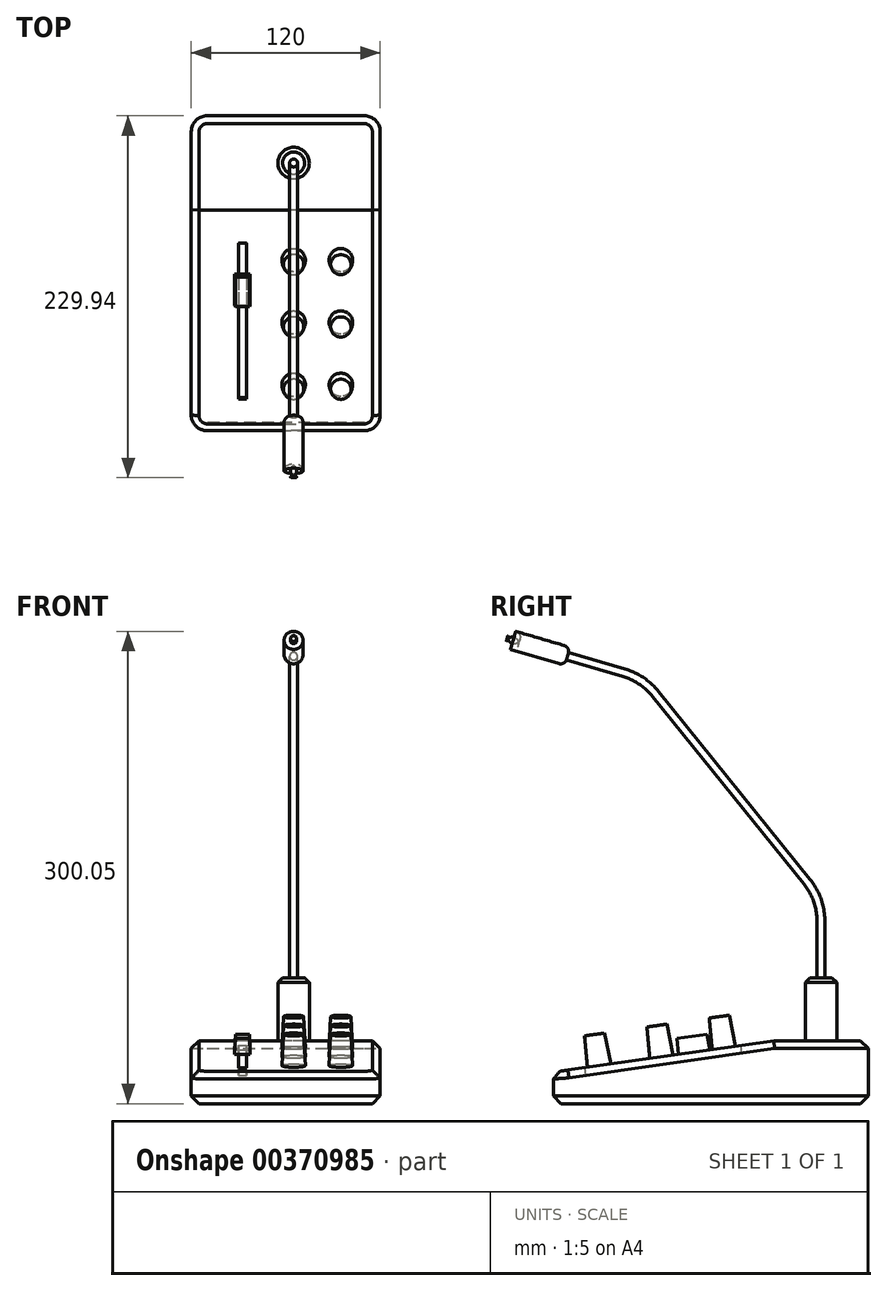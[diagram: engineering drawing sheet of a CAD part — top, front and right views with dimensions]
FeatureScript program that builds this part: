
annotation { "Feature Type Name" : "Feature", "Feature Type Description" : "" }
export const myFeature = defineFeature(function(context is Context, id is Id, definition is map)
    precondition{}
    {
        {
            var Q0;
            Q0=qCreatedBy(makeId("Right.planeOp"),FACE);
            var sketch = newSketch(context, id + "F0", { "sketchPlane" : qUnion([Q0])});
            skLineSegment(sketch, "E0", {"start": v(-86.5, 0) * mm, "end": v(113.5, 0) * mm});
            skLineSegment(sketch, "E1", {"start": v(113.5, 0) * mm, "end": v(113.5, 40) * mm});
            skLineSegment(sketch, "E2", {"start": v(113.5, 40) * mm, "end": v(53.5, 40) * mm});
            skLineSegment(sketch, "E3", {"start": v(53.5, 40) * mm, "end": v(-86.5, 20) * mm});
            skLineSegment(sketch, "E4", {"start": v(-86.5, 20) * mm, "end": v(-86.5, 0) * mm});
            skSolve(sketch);
        }
        {
            var Q0;
            Q0 = qSketchRegion(id + "F0", true);
            extrude(context, id + "F1", {"entities" : qUnion([Q0]), "endBound" : BoundingType.SYMMETRIC, "depth" : 120 * mm});
        }
        {
            var Q0;
            Q0=makeQuery(id+"F1.opExtrude","CAP_EDGE",EDGE,{"disambiguationData":[OSD([sQuery(id+"F0.wireOp",EDGE,"E4")])],"isStart":true});
            var Q1;
            Q1=makeQuery(id+"F1.opExtrude","CAP_EDGE",EDGE,{"disambiguationData":[OSD([sQuery(id+"F0.wireOp",EDGE,"E4")])],"isStart":false});
            var Q2;
            Q2=makeQuery(id+"F1.opExtrude","CAP_EDGE",EDGE,{"disambiguationData":[OSD([sQuery(id+"F0.wireOp",EDGE,"E1")])],"isStart":false});
            var Q3;
            Q3=makeQuery(id+"F1.opExtrude","CAP_EDGE",EDGE,{"disambiguationData":[OSD([sQuery(id+"F0.wireOp",EDGE,"E1")])],"isStart":true});
            fillet(context, id + "F2", {"entities" : qUnion([Q0, Q1, Q2, Q3]), "radius" : 10 * mm, "tangentPropagation" : true, "allowEdgeOverflow" : false});
        }
        {
            var Q0;
            Q0=makeQuery(id+"F1.opExtrude","CAP_EDGE",EDGE,{"disambiguationData":[OSD([sQuery(id+"F0.wireOp",EDGE,"E0")])],"isStart":true});
            var Q1;
            Q1=makeQuery(id+"F1.opExtrude","CAP_EDGE",EDGE,{"disambiguationData":[OSD([sQuery(id+"F0.wireOp",EDGE,"E3")])],"isStart":false});
            var Q2;
            Q2=makeQuery(id+"F1.opExtrude","CAP_EDGE",EDGE,{"disambiguationData":[OSD([sQuery(id+"F0.wireOp",EDGE,"E2")])],"isStart":false});
            chamfer(context, id + "F3", {"entities" : qUnion([Q0, Q1, Q2]), "width" : 5 * mm, "tangentPropagation" : true});
        }
        {
            var Q0;
            Q0=makeQuery(id+"F1.opExtrude","SWEPT_FACE",FACE,{"disambiguationData":[OSD([sQuery(id+"F0.wireOp",EDGE,"E3")])]});
            var sketch = newSketch(context, id + "F4", { "sketchPlane" : qUnion([Q0])});
            skLineSegment(sketch, "E5.bottom", {"start": v(-30, 37.58) * mm, "end": v(-25, 37.58) * mm});
            skLineSegment(sketch, "E5.top", {"start": v(-30, -62.42) * mm, "end": v(-25, -62.42) * mm});
            skLineSegment(sketch, "E5.left", {"start": v(-30, 37.58) * mm, "end": v(-30, -62.42) * mm});
            skLineSegment(sketch, "E5.right", {"start": v(-25, 37.58) * mm, "end": v(-25, -62.42) * mm});
            skSolve(sketch);
        }
        {
            var Q0;
            Q0 = qSketchRegion(id + "F4", true);
            extrude(context, id + "F5", {"entities" : qUnion([Q0]), "operationType" : NewBodyOperationType.REMOVE, "oppositeDirection" : true, "depth" : 5 * mm});
        }
        {
            var Q0;
            Q0=makeQuery(id+"F1.opExtrude","SWEPT_FACE",FACE,{"disambiguationData":[OSD([sQuery(id+"F0.wireOp",EDGE,"E3")])]});
            var sketch = newSketch(context, id + "F6", { "sketchPlane" : qUnion([Q0])});
            skLineSegment(sketch, "E6.bottom", {"start": v(-32.5, 17.58) * mm, "end": v(-22.5, 17.58) * mm});
            skLineSegment(sketch, "E6.top", {"start": v(-32.5, -2.42) * mm, "end": v(-22.5, -2.42) * mm});
            skLineSegment(sketch, "E6.left", {"start": v(-32.5, 17.58) * mm, "end": v(-32.5, -2.42) * mm});
            skLineSegment(sketch, "E6.right", {"start": v(-22.5, 17.58) * mm, "end": v(-22.5, -2.42) * mm});
            skSolve(sketch);
        }
        {
            var Q0;
            Q0 = qSketchRegion(id + "F6", true);
            extrude(context, id + "F7", {"entities" : qUnion([Q0]), "operationType" : NewBodyOperationType.ADD, "depth" : 10 * mm, "hasDraft" : true, "draftAngle" : 3 * degree, "draftPullDirection" : true});
        }
        {
            var Q0;
            Q0=makeQuery(id+"F1.opExtrude","SWEPT_FACE",FACE,{"disambiguationData":[OSD([sQuery(id+"F0.wireOp",EDGE,"E3")])]});
            var sketch = newSketch(context, id + "F8", { "sketchPlane" : qUnion([Q0])});
            skCircle(sketch, "E7", {"center": v(35, -53.42) * mm, "radius": 7.5 * mm});
            skCircle(sketch, "E8.0.1.0", {"center": v(35, -13.42) * mm, "radius": 7.5 * mm});
            skCircle(sketch, "E8.0.2.0", {"center": v(35, 26.58) * mm, "radius": 7.5 * mm});
            skCircle(sketch, "E8.1.0.0", {"center": v(5, -53.42) * mm, "radius": 7.5 * mm});
            skCircle(sketch, "E8.1.1.0", {"center": v(5, -13.42) * mm, "radius": 7.5 * mm});
            skCircle(sketch, "E8.1.2.0", {"center": v(5, 26.58) * mm, "radius": 7.5 * mm});
            skLineSegment(sketch, "E8.direction1", {"start": v(35, -53.42) * mm, "end": v(5, -53.42) * mm, "construction": true});
            skLineSegment(sketch, "E8.direction2", {"start": v(35, -53.42) * mm, "end": v(35, -13.42) * mm, "construction": true});
            skSolve(sketch);
        }
        {
            var Q0;
            Q0 = qSketchRegion(id + "F8", true);
            extrude(context, id + "F9", {"entities" : qUnion([Q0]), "operationType" : NewBodyOperationType.ADD, "depth" : 20 * mm, "hasDraft" : true, "draftAngle" : 3 * degree, "draftPullDirection" : true});
        }
        {
            var Q0;
            Q0=makeQuery(id+"F1.opExtrude","SWEPT_FACE",FACE,{"disambiguationData":[OSD([sQuery(id+"F0.wireOp",EDGE,"E2")])]});
            var sketch = newSketch(context, id + "F10", { "sketchPlane" : qUnion([Q0])});
            skCircle(sketch, "E9", {"center": v(5, 83.5) * mm, "radius": 10 * mm});
            skSolve(sketch);
        }
        {
            var Q0;
            Q0 = qSketchRegion(id + "F10", true);
            extrude(context, id + "F11", {"entities" : qUnion([Q0]), "operationType" : NewBodyOperationType.ADD, "depth" : 40 * mm});
        }
        {
            var Q0;
            Q0=makeQuery(id+"F11.opExtrude","CAP_EDGE",EDGE,{"disambiguationData":[OSD([sQuery(id+"F10.wireOp",EDGE,"E9")])],"isStart":false});
            chamfer(context, id + "F12", {"entities" : qUnion([Q0]), "width" : 3 * mm, "tangentPropagation" : true});
        }
        {
            var Q0;
            {var subQ0=sQuery(id+"F10.wireOp",EDGE,"E9");Q0=makeQuery(id+"F12.opChamfer","BLEND_EDGE",EDGE,{"blendedFrom":[makeQuery(id+"F11.opExtrude","CAP_EDGE",EDGE,{"disambiguationData":[OSD([subQ0])],"isStart":false}),makeQuery(id+"F11.opExtrude","CAP_FACE",FACE,{"disambiguationData":[OSD([subQ0])],"isStart":false})],"blendedInto":[makeQuery(id+"F11.opExtrude","CAP_FACE",FACE,{"disambiguationData":[OSD([subQ0])],"isStart":false})]});}
            cPlane(context, id + "F13", {"entities" : qUnion([Q0]), "cplaneType" : CPlaneType.LINE_ANGLE, "offset" : 25 * mm, "angle" : 0 * degree, "width" : 150 * mm, "height" : 150 * mm});
        }
        {
            var Q0;
            Q0=qCreatedBy(id+"F13.planeOp",FACE);
            var sketch = newSketch(context, id + "F14", { "sketchPlane" : qUnion([Q0])});
            skLineSegment(sketch, "E10", {"start": v(83.5, 80) * mm, "end": v(83.5, 115.88) * mm});
            skLineSegment(sketch, "E11", {"start": v(74.63, 141) * mm, "end": v(-21.65, 260.35) * mm});
            skLineSegment(sketch, "E12", {"start": v(-41.54, 273.63) * mm, "end": v(-77.5, 284.17) * mm});
            skPoint(sketch, "E13.visualSharp", {"position": v(-29.52, 270.1) * mm});
            skArc(sketch, "E13.filletArc", {"start": v(-21.65, 260.35) * mm, "mid": v(-30.58, 268.51) * mm, "end": v(-41.54, 273.63) * mm});
            skPoint(sketch, "E14.visualSharp", {"position": v(83.5, 130) * mm});
            skArc(sketch, "E14.filletArc", {"start": v(83.5, 115.88) * mm, "mid": v(81.21, 129.2) * mm, "end": v(74.63, 141) * mm});
            skSolve(sketch);
        }
        {
            var Q0;
            Q0=makeQuery(id+"F11.opExtrude","CAP_FACE",FACE,{"disambiguationData":[OSD([sQuery(id+"F10.wireOp",EDGE,"E9")])],"isStart":false});
            var sketch = newSketch(context, id + "F15", { "sketchPlane" : qUnion([Q0])});
            skCircle(sketch, "E15", {"center": v(5, 83.5) * mm, "radius": 2.5 * mm});
            skSolve(sketch);
        }
        {
            var Q0;
            Q0 = qSketchRegion(id + "F15", true);
            var Q1;
            Q1 = qConstructionFilter(qBodyType(qCreatedBy(id + "F14" ,EDGE), BodyType.WIRE), ConstructionObject.NO);
            sweep(context, id + "F16", {"operationType" : NewBodyOperationType.ADD, "profiles" : qUnion([Q0]), "path" : qUnion([Q1])});
        }
        {
            var Q0;
            Q0=makeQuery(id+"F16.opSweep","CAP_FACE",FACE,{"disambiguationData":[OSD([sQuery(id+"F14.wireOp",VERTEX,"E12.end"),sQuery(id+"F15.wireOp",EDGE,"E15")])],"isStart":false});
            var sketch = newSketch(context, id + "F17", { "sketchPlane" : qUnion([Q0])});
            skCircle(sketch, "E16", {"center": v(5, 250.9) * mm, "radius": 6 * mm});
            skSolve(sketch);
        }
        {
            var Q0;
            Q0 = qSketchRegion(id + "F17", true);
            extrude(context, id + "F18", {"entities" : qUnion([Q0]), "operationType" : NewBodyOperationType.ADD, "depth" : 40 * mm});
        }
        {
            var Q0;
            Q0=makeQuery(id+"F18.opExtrude","CAP_EDGE",EDGE,{"disambiguationData":[OSD([sQuery(id+"F17.wireOp",EDGE,"E16")])],"isStart":false});
            var Q1;
            Q1=makeQuery(id+"F18.opExtrude","CAP_EDGE",EDGE,{"disambiguationData":[OSD([sQuery(id+"F17.wireOp",EDGE,"E16")])],"isStart":true});
            fillet(context, id + "F19", {"entities" : qUnion([Q0, Q1]), "radius" : 4 * mm, "tangentPropagation" : true, "allowEdgeOverflow" : false});
        }
    });
